# Revit family: P200921MX-079c_MGD8230HC
name_source: partatom
category: Specialty Equipment
units: mm (PartAtom-declared; Revit-internal decimal feet)

## family parameters
Always vertical = Yes
Cut with Voids When Loaded = No
Enable Cutting in Views = No
Maintain Annotation Orientation = No
Part Type = Normal
Room Calculation Point = No
Round Connector Dimension = Use Diameter
Shared = No
Work Plane-Based = No

## types (1)
- MGD8230HC
    Accent Material = ARCAT - Plastic, ABS - Black
    Amps = 0 A
    Back Panel Material = ARCAT - Metal - Aluminum
    Body Material = ARCAT - Metal - Steel - Gray
    Clearance Material = ARCAT - Clearance
    Default Elevation = 0"
    Depth = 32 3/4"
    Description = Smart Capable Top Load Gas Dryer with Extra Power Button - 8.8 cu. ft.
Sécheuse intelligente à chargement vertical, Extra Power, 8,8 pi³
    Dimension Guide = https://www.whirlpool.com
    Display Material = ARCAT - Glass - Tempered - Dark Black
    Display Panel Material = ARCAT - Metal - Steel - Dark - Gray
    Door Material = ARCAT - Metal - Steel - Stainless
    Family Name = Laundry
    Feature 1 = Extra Power button
Extra Power button
    Feature 2 = Advanced Moisture Sensing Plus
Détection d'humidité perfectionnée avec capteur additionnel d’humidité, exclusif dans l’industrie.
    Feature 3 = Smart capable appliance
Électroménager intelligent
    Glass Material = ARCAT - Glass - Tempered - Black
    Handle Material = ARCAT - Metal - Steel - Stainless
    Height = 42 3/4"
    Knob Material = ARCAT - Metal - Steel - Stainless
    Leg Material = ARCAT - Plastic - White
    Manufacturer = Maytag
    Model = MGD8230HC
    Voltage = 0 V
    Width = 29"

## geometry (parser evidence)
native form markers: Sweep x5
no freeform markers — native parametric forms only
